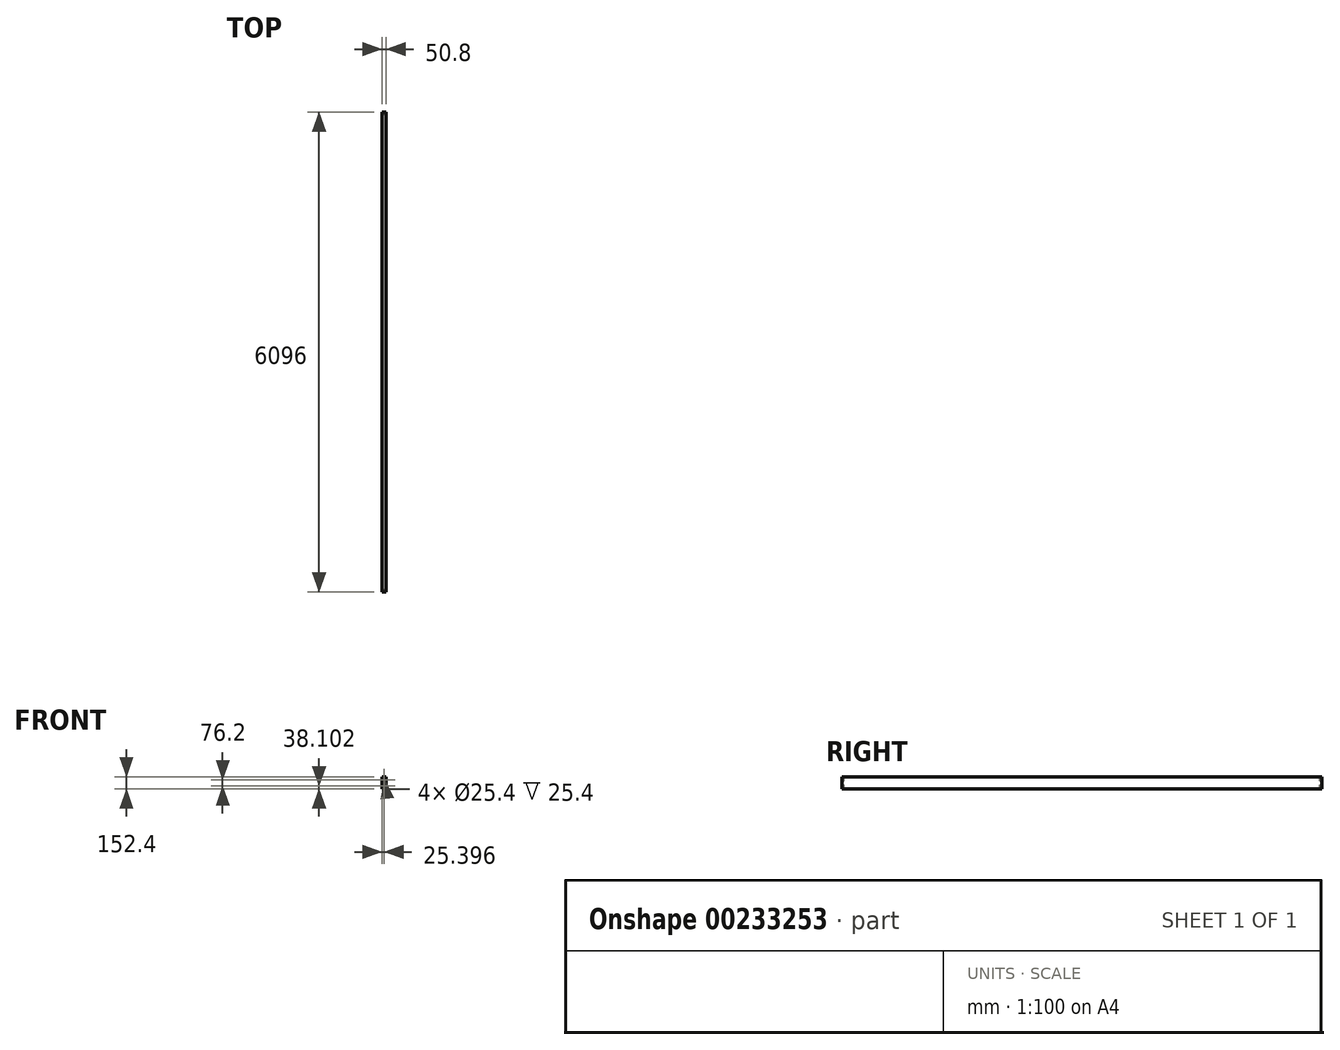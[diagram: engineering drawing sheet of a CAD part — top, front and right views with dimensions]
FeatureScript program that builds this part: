
annotation { "Feature Type Name" : "Feature", "Feature Type Description" : "" }
export const myFeature = defineFeature(function(context is Context, id is Id, definition is map)
    precondition{}
    {
        {
            var Q0;
            Q0=qCreatedBy(makeId("Front.planeOp"),FACE);
            var sketch = newSketch(context, id + "F0", { "sketchPlane" : qUnion([Q0])});
            skLineSegment(sketch, "E0.bottom", {"start": v(-58.98, 101.93) * mm, "end": v(-8.18, 101.93) * mm});
            skLineSegment(sketch, "E0.top", {"start": v(-58.98, -50.47) * mm, "end": v(-8.18, -50.47) * mm});
            skLineSegment(sketch, "E0.left", {"start": v(-58.98, 101.93) * mm, "end": v(-58.98, -50.47) * mm});
            skLineSegment(sketch, "E0.right", {"start": v(-8.18, 101.93) * mm, "end": v(-8.18, -50.47) * mm});
            skCircle(sketch, "E1", {"center": v(-33.58, 63.83) * mm, "radius": 12.7 * mm});
            skCircle(sketch, "E2", {"center": v(-33.58, -12.37) * mm, "radius": 12.7 * mm});
            skSolve(sketch);
        }
        {
            var Q0;
            Q0 = qSketchRegion(id + "F0", true);
            extrude(context, id + "F1", {"entities" : qUnion([Q0]), "depth" : 6096 * mm});
        }
        {
            var Q0;
            Q0=makeQuery(id+"F0.imprint","IMPRINT",FACE,{"disambiguationData":[TD([[makeQuery(id+"F0.imprint","IMPRINT",EDGE,{"derivedFrom":sQuery(id+"F0.wireOp",EDGE,"E1")}),1.0]])]});
            var Q1;
            Q1=makeQuery(id+"F0.imprint","IMPRINT",FACE,{"disambiguationData":[TD([[makeQuery(id+"F0.imprint","IMPRINT",EDGE,{"derivedFrom":sQuery(id+"F0.wireOp",EDGE,"E2")}),1.0]])]});
            extrude(context, id + "F2", {"entities" : qUnion([Q0, Q1]), "operationType" : NewBodyOperationType.ADD, "depth" : 6070.6 * mm});
        }
        {
            var Q0;
            Q0=makeQuery(id+"F0.imprint","IMPRINT",FACE,{"disambiguationData":[TD([[makeQuery(id+"F0.imprint","IMPRINT",EDGE,{"derivedFrom":sQuery(id+"F0.wireOp",EDGE,"E1")}),1.0]])]});
            var Q1;
            Q1=makeQuery(id+"F0.imprint","IMPRINT",FACE,{"disambiguationData":[TD([[makeQuery(id+"F0.imprint","IMPRINT",EDGE,{"derivedFrom":sQuery(id+"F0.wireOp",EDGE,"E2")}),1.0]])]});
            extrude(context, id + "F3", {"entities" : qUnion([Q0, Q1]), "operationType" : NewBodyOperationType.REMOVE, "depth" : 25.4 * mm});
        }
    });
